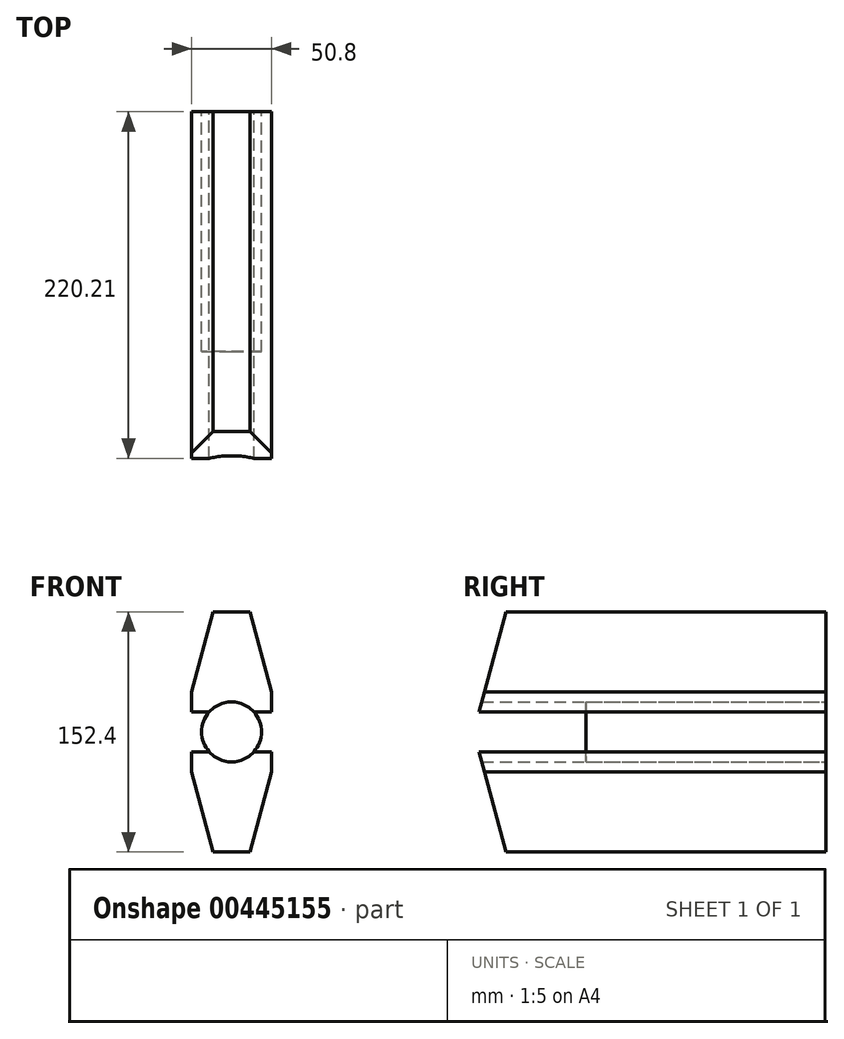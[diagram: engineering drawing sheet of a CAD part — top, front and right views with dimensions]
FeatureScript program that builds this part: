
annotation { "Feature Type Name" : "Feature", "Feature Type Description" : "" }
export const myFeature = defineFeature(function(context is Context, id is Id, definition is map)
    precondition{}
    {
        {
            var Q0;
            Q0=qCreatedBy(makeId("Right.planeOp"),FACE);
            var sketch = newSketch(context, id + "F0", { "sketchPlane" : qUnion([Q0])});
            skLineSegment(sketch, "E0", {"start": v(0, 0) * mm, "end": v(0, 63.5) * mm});
            skLineSegment(sketch, "E1", {"start": v(0, 63.5) * mm, "end": v(-203.2, 63.5) * mm});
            skLineSegment(sketch, "E2", {"start": v(0, 0) * mm, "end": v(-220.21, 0) * mm});
            skLineSegment(sketch, "E3", {"start": v(-203.2, 63.5) * mm, "end": v(-220.21, 0) * mm});
            skLineSegment(sketch, "E4", {"start": v(0, 0) * mm, "end": v(0, -25.4) * mm});
            skLineSegment(sketch, "E5", {"start": v(0, -25.4) * mm, "end": v(0, -88.9) * mm});
            skLineSegment(sketch, "E6", {"start": v(0, -88.9) * mm, "end": v(-203.2, -88.9) * mm});
            skLineSegment(sketch, "E7", {"start": v(0, -25.4) * mm, "end": v(-220.21, -25.4) * mm});
            skLineSegment(sketch, "E8", {"start": v(-220.21, -25.4) * mm, "end": v(-203.2, -88.9) * mm});
            skSolve(sketch);
        }
        {
            var Q0;
            Q0=makeQuery(id+"F0.imprint","IMPRINT",FACE,{"disambiguationData":[TD([[makeQuery(id+"F0.imprint","IMPRINT",EDGE,{"derivedFrom":sQuery(id+"F0.wireOp",EDGE,"E0")}),1.0]])]});
            var Q1;
            Q1=makeQuery(id+"F0.imprint","IMPRINT",FACE,{"disambiguationData":[TD([[makeQuery(id+"F0.imprint","IMPRINT",EDGE,{"derivedFrom":sQuery(id+"F0.wireOp",EDGE,"E5")}),-1.0]])]});
            extrude(context, id + "F1", {"entities" : qUnion([Q0, Q1]), "endBound" : BoundingType.SYMMETRIC, "depth" : 50.8 * mm});
        }
        {
            var Q0;
            Q0=qCreatedBy(makeId("Front.planeOp"),FACE);
            var sketch = newSketch(context, id + "F2", { "sketchPlane" : qUnion([Q0])});
            skLineSegment(sketch, "E9.0", {"start": v(25.4, 0) * mm, "end": v(-25.4, 0) * mm});
            skLineSegment(sketch, "E10.0", {"start": v(25.4, -25.4) * mm, "end": v(-25.4, -25.4) * mm});
            skLineSegment(sketch, "E11", {"start": v(0, 0) * mm, "end": v(0, -25.4) * mm});
            skCircle(sketch, "E12", {"center": v(0, -12.7) * mm, "radius": 22.23 * mm});
            skCircle(sketch, "E13", {"center": v(0, -12.7) * mm, "radius": 19.05 * mm});
            skSolve(sketch);
        }
        {
            var Q0;
            {var subQ0=sQuery(id+"F2.wireOp",EDGE,"E11");Q0=makeQuery(id+"F2.imprint","IMPRINT",FACE,{"disambiguationData":[TD([[makeQuery(id+"F2.imprint","IMPRINT",EDGE,{"derivedFrom":subQ0}),-1.0]])]});}
            var Q1;
            {var subQ0=sQuery(id+"F2.wireOp",EDGE,"E11");Q1=makeQuery(id+"F2.imprint","IMPRINT",FACE,{"disambiguationData":[TD([[makeQuery(id+"F2.imprint","IMPRINT",EDGE,{"derivedFrom":subQ0}),1.0]])]});}
            var Q2;
            {var subQ0=sQuery(id+"F2.wireOp",EDGE,"E10.0");var subQ1=makeQuery(id+"F2.imprint","INTERSECT",VERTEX,{"derivedFrom":[subQ0,sQuery(id+"F2.wireOp",EDGE,"E11")]});Q2=makeQuery(id+"F2.imprint","IMPRINT",FACE,{"disambiguationData":[TD([[makeQuery(id+"F2.imprint","IMPRINT",EDGE,{"disambiguationData":[TD([[subQ1,1.0]])],"derivedFrom":subQ0}),1.0]])]});}
            var Q3;
            {var subQ0=sQuery(id+"F2.wireOp",EDGE,"E9.0");var subQ1=makeQuery(id+"F2.imprint","INTERSECT",VERTEX,{"derivedFrom":[subQ0,sQuery(id+"F2.wireOp",EDGE,"E11")]});Q3=makeQuery(id+"F2.imprint","IMPRINT",FACE,{"disambiguationData":[TD([[makeQuery(id+"F2.imprint","IMPRINT",EDGE,{"disambiguationData":[TD([[subQ1,1.0]])],"derivedFrom":subQ0}),-1.0]])]});}
            var Q4;
            Q4=makeQuery(id+"F1.opExtrude","SWEPT_FACE",FACE,{"disambiguationData":[OSD([sQuery(id+"F0.wireOp",EDGE,"E3")])]});
            var Q5;
            {var subQ0=sQuery(id+"F2.wireOp",EDGE,"E12");var subQ1=sQuery(id+"F2.wireOp",EDGE,"E9.0");var subQ2=makeQuery(id+"F2.imprint","INTERSECT",VERTEX,{"disambiguationData":[OD(0.0)],"derivedFrom":[subQ1,subQ0]});Q5=makeQuery(id+"F2.imprint","IMPRINT",FACE,{"disambiguationData":[TD([[makeQuery(id+"F2.imprint","IMPRINT",EDGE,{"disambiguationData":[TD([[subQ2,-1.0]])],"derivedFrom":subQ1}),1.0]])]});}
            var Q6;
            {var subQ0=sQuery(id+"F2.wireOp",EDGE,"E12");var subQ1=sQuery(id+"F2.wireOp",EDGE,"E9.0");var subQ2=makeQuery(id+"F2.imprint","INTERSECT",VERTEX,{"disambiguationData":[OD(1.0)],"derivedFrom":[subQ1,subQ0]});Q6=makeQuery(id+"F2.imprint","IMPRINT",FACE,{"disambiguationData":[TD([[makeQuery(id+"F2.imprint","IMPRINT",EDGE,{"disambiguationData":[TD([[subQ2,1.0]])],"derivedFrom":subQ1}),1.0]])]});}
            var Q7;
            {var subQ0=sQuery(id+"F2.wireOp",EDGE,"E12");var subQ1=sQuery(id+"F2.wireOp",EDGE,"E9.0");var subQ2=makeQuery(id+"F2.imprint","INTERSECT",VERTEX,{"disambiguationData":[OD(0.0)],"derivedFrom":[subQ1,subQ0]});Q7=makeQuery(id+"F2.imprint","IMPRINT",FACE,{"disambiguationData":[TD([[makeQuery(id+"F2.imprint","IMPRINT",EDGE,{"disambiguationData":[TD([[subQ2,-1.0]])],"derivedFrom":subQ1}),-1.0]])]});}
            var Q8;
            {var subQ0=sQuery(id+"F2.wireOp",EDGE,"E12");var subQ1=sQuery(id+"F2.wireOp",EDGE,"E10.0");var subQ2=makeQuery(id+"F2.imprint","INTERSECT",VERTEX,{"disambiguationData":[OD(0.0)],"derivedFrom":[subQ1,subQ0]});Q8=makeQuery(id+"F2.imprint","IMPRINT",FACE,{"disambiguationData":[TD([[makeQuery(id+"F2.imprint","IMPRINT",EDGE,{"disambiguationData":[TD([[subQ2,-1.0]])],"derivedFrom":subQ1}),1.0]])]});}
            var Q9;
            Q9=makeQuery(id+"F1.opExtrude","SWEPT_FACE",FACE,{"disambiguationData":[OSD([sQuery(id+"F0.wireOp",EDGE,"E3")])]});
            extrude(context, id + "F3", {"entities" : qUnion([Q0, Q1, Q2, Q3, Q4, Q5, Q6, Q7, Q8]), "operationType" : NewBodyOperationType.REMOVE, "endBound" : BoundingType.THROUGH_ALL, "endBoundEntityFace" : qUnion([Q9]), "depth" : 25.4 * mm});
        }
        {
            var Q0;
            Q0=qCreatedBy(makeId("Front.planeOp"),FACE);
            var sketch = newSketch(context, id + "F4", { "sketchPlane" : qUnion([Q0])});
            skLineSegment(sketch, "E14.0", {"start": v(25.4, 63.5) * mm, "end": v(25.4, 0) * mm});
            skLineSegment(sketch, "E15.0", {"start": v(25.4, -25.4) * mm, "end": v(25.4, -88.9) * mm});
            skLineSegment(sketch, "E16.0", {"start": v(-25.4, -25.4) * mm, "end": v(-25.4, -88.9) * mm});
            skLineSegment(sketch, "E17.0", {"start": v(-25.4, 63.5) * mm, "end": v(-25.4, 0) * mm});
            skLineSegment(sketch, "E18.0", {"start": v(25.4, 63.5) * mm, "end": v(-25.4, 63.5) * mm});
            skLineSegment(sketch, "E19.0", {"start": v(25.4, -88.9) * mm, "end": v(-25.4, -88.9) * mm});
            skLineSegment(sketch, "E20", {"start": v(-25.4, 63.5) * mm, "end": v(-11.79, 63.5) * mm});
            skLineSegment(sketch, "E21", {"start": v(-25.4, 0) * mm, "end": v(-25.4, 12.7) * mm});
            skLineSegment(sketch, "E22", {"start": v(-25.4, 12.7) * mm, "end": v(-11.79, 63.5) * mm});
            skLineSegment(sketch, "E23", {"start": v(0, 63.5) * mm, "end": v(0, 53.22) * mm});
            skPoint(sketch, "E23.endSnap0", {"position": v(0, 63.5) * mm});
            skLineSegment(sketch, "E24.MirrorCS", {"start": v(25.4, 12.7) * mm, "end": v(11.79, 63.5) * mm});
            skLineSegment(sketch, "E25", {"start": v(25.4, 0) * mm, "end": v(25.4, -25.4) * mm});
            skLineSegment(sketch, "E26", {"start": v(25.4, -12.7) * mm, "end": v(14.87, -12.7) * mm});
            skLineSegment(sketch, "E27.MirrorCS", {"start": v(25.4, -38.1) * mm, "end": v(11.79, -88.9) * mm});
            skLineSegment(sketch, "E28.MirrorCS", {"start": v(-25.4, -38.1) * mm, "end": v(-11.79, -88.9) * mm});
            skSolve(sketch);
        }
        {
            var Q0;
            {var subQ3=sQuery(id+"F4.wireOp",EDGE,"E28.MirrorCS");Q0=makeQuery(id+"F4.imprint","IMPRINT",FACE,{"disambiguationData":[TD([[makeQuery(id+"F4.imprint","IMPRINT",EDGE,{"derivedFrom":subQ3}),-1.0]])]});}
            var Q1;
            {var subQ3=sQuery(id+"F4.wireOp",EDGE,"E27.MirrorCS");Q1=makeQuery(id+"F4.imprint","IMPRINT",FACE,{"disambiguationData":[TD([[makeQuery(id+"F4.imprint","IMPRINT",EDGE,{"derivedFrom":subQ3}),1.0]])]});}
            var Q2;
            {var subQ3=sQuery(id+"F4.wireOp",EDGE,"E24.MirrorCS");Q2=makeQuery(id+"F4.imprint","IMPRINT",FACE,{"disambiguationData":[TD([[makeQuery(id+"F4.imprint","IMPRINT",EDGE,{"derivedFrom":subQ3}),-1.0]])]});}
            var Q3;
            Q3=makeQuery(id+"F4.imprint","IMPRINT",FACE,{"disambiguationData":[TD([[makeQuery(id+"F4.imprint","IMPRINT",EDGE,{"derivedFrom":sQuery(id+"F4.wireOp",EDGE,"E17.0")}),1.0]])]});
            extrude(context, id + "F5", {"entities" : qUnion([Q0, Q1, Q2, Q3]), "operationType" : NewBodyOperationType.REMOVE, "endBound" : BoundingType.THROUGH_ALL, "depth" : 25.4 * mm});
        }
        {
            var Q0;
            {var subQ0=sQuery(id+"F2.wireOp",EDGE,"E11");Q0=makeQuery(id+"F2.imprint","IMPRINT",FACE,{"disambiguationData":[TD([[makeQuery(id+"F2.imprint","IMPRINT",EDGE,{"derivedFrom":subQ0}),-1.0]])]});}
            var Q1;
            {var subQ0=sQuery(id+"F2.wireOp",EDGE,"E11");Q1=makeQuery(id+"F2.imprint","IMPRINT",FACE,{"disambiguationData":[TD([[makeQuery(id+"F2.imprint","IMPRINT",EDGE,{"derivedFrom":subQ0}),1.0]])]});}
            var Q2;
            {var subQ0=sQuery(id+"F2.wireOp",EDGE,"E9.0");var subQ1=makeQuery(id+"F2.imprint","INTERSECT",VERTEX,{"derivedFrom":[subQ0,sQuery(id+"F2.wireOp",EDGE,"E11")]});Q2=makeQuery(id+"F2.imprint","IMPRINT",FACE,{"disambiguationData":[TD([[makeQuery(id+"F2.imprint","IMPRINT",EDGE,{"disambiguationData":[TD([[subQ1,1.0]])],"derivedFrom":subQ0}),-1.0]])]});}
            var Q3;
            {var subQ0=sQuery(id+"F2.wireOp",EDGE,"E10.0");var subQ1=makeQuery(id+"F2.imprint","INTERSECT",VERTEX,{"derivedFrom":[subQ0,sQuery(id+"F2.wireOp",EDGE,"E11")]});Q3=makeQuery(id+"F2.imprint","IMPRINT",FACE,{"disambiguationData":[TD([[makeQuery(id+"F2.imprint","IMPRINT",EDGE,{"disambiguationData":[TD([[subQ1,1.0]])],"derivedFrom":subQ0}),1.0]])]});}
            extrude(context, id + "F6", {"entities" : qUnion([Q0, Q1, Q2, Q3]), "depth" : 152.4 * mm});
        }
    });
